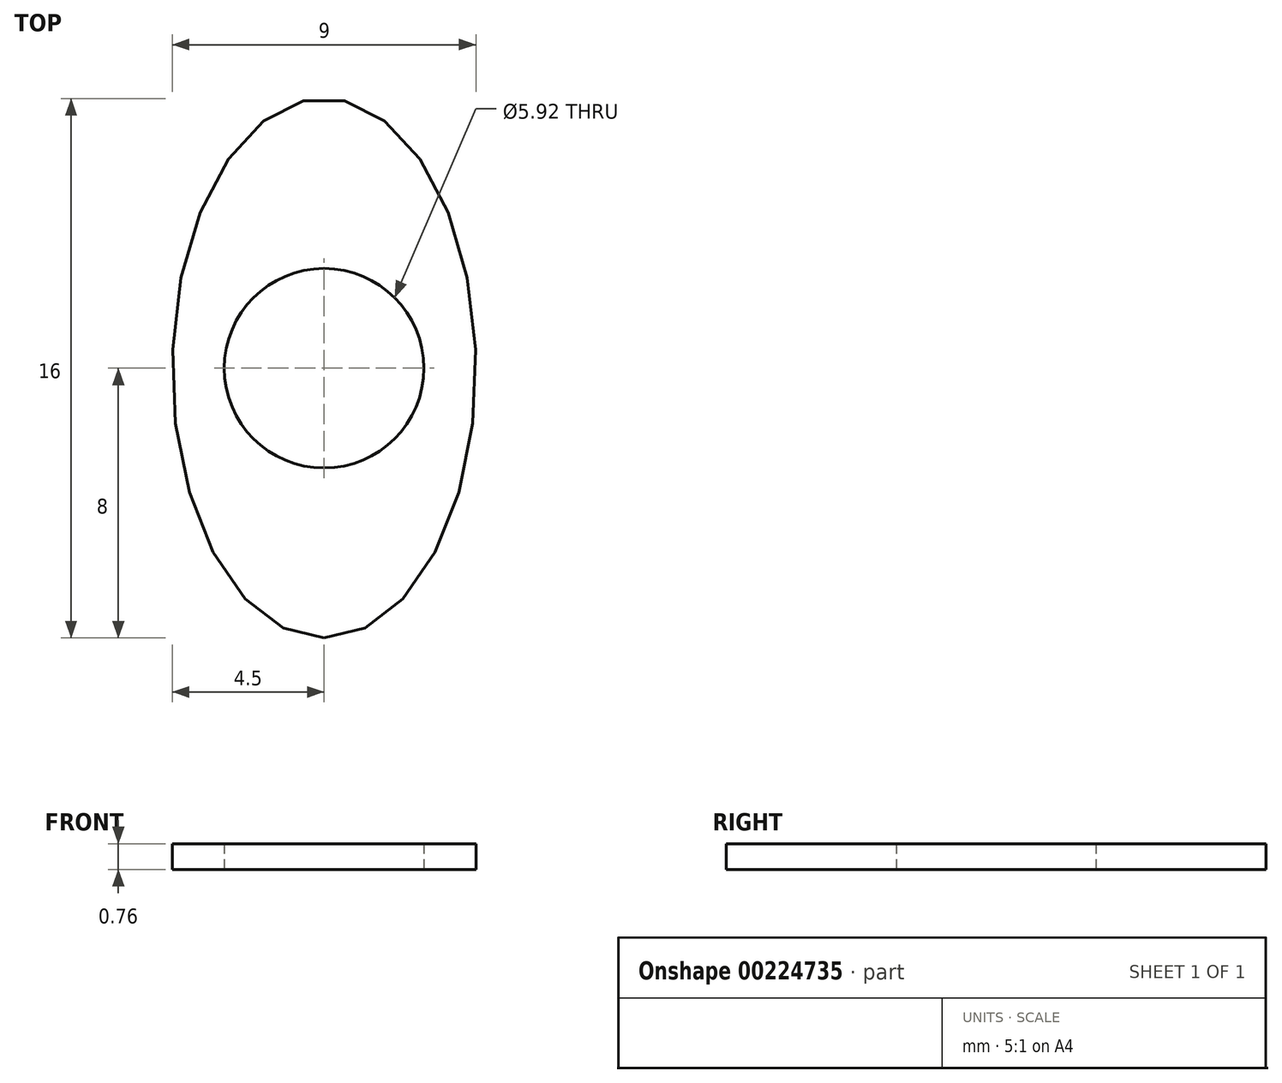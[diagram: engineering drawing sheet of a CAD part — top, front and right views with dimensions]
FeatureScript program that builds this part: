
annotation { "Feature Type Name" : "Feature", "Feature Type Description" : "" }
export const myFeature = defineFeature(function(context is Context, id is Id, definition is map)
    precondition{}
    {
        {
            var Q0;
            Q0=qCreatedBy(makeId("Top.planeOp"),FACE);
            var sketch = newSketch(context, id + "F0", { "sketchPlane" : qUnion([Q0])});
            skCircle(sketch, "E0", {"center": v(0, 0) * mm, "radius": 2.96 * mm});
            skEllipse(sketch, "E1", {"center": v(0, 0) * mm, "majorRadius": 8 * mm, "minorRadius": 4.5 * mm, "majorAxis": v(0, -1)});
            skSolve(sketch);
        }
        {
            var Q0;
            Q0=qSketchRegion(id+"F0",true);
            extrude(context, id + "F1", {"entities" : qUnion([Q0]), "endBound" : BoundingType.SYMMETRIC, "depth" : 0.76 * mm});
        }
    });
